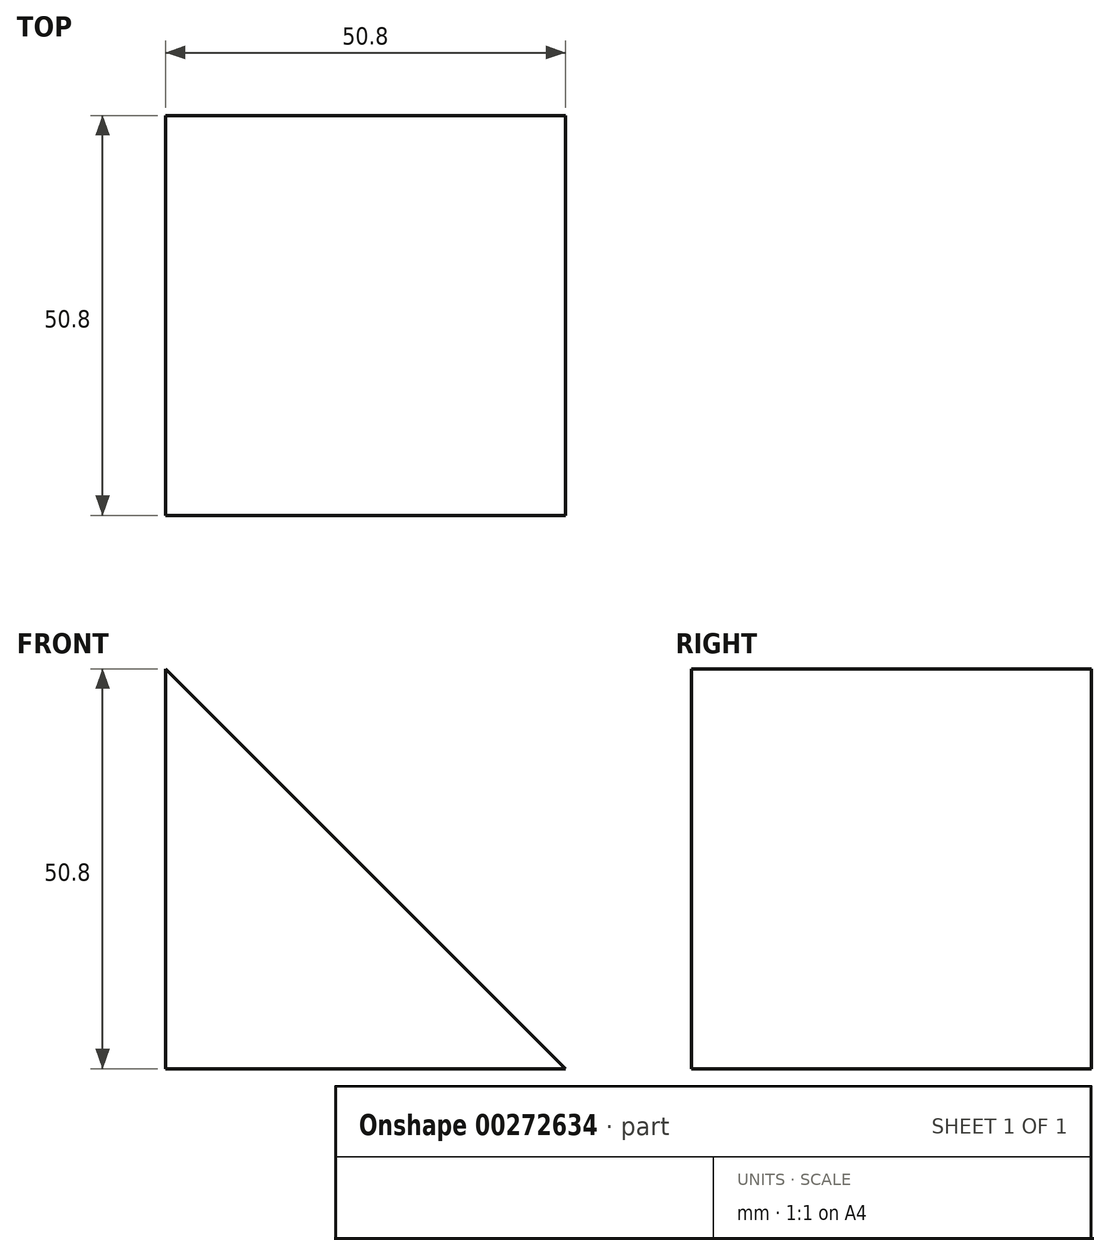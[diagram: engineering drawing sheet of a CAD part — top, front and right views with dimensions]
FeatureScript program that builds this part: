
annotation { "Feature Type Name" : "Feature", "Feature Type Description" : "" }
export const myFeature = defineFeature(function(context is Context, id is Id, definition is map)
    precondition{}
    {
        {
            var Q0;
            Q0=qCreatedBy(makeId("Front.planeOp"),FACE);
            var sketch = newSketch(context, id + "F0", { "sketchPlane" : qUnion([Q0])});
            skLineSegment(sketch, "E0.top", {"start": v(-43.73, -47.36) * mm, "end": v(7.07, -47.36) * mm});
            skLineSegment(sketch, "E0.left", {"start": v(-43.73, 3.44) * mm, "end": v(-43.73, -47.36) * mm});
            skLineSegment(sketch, "E1", {"start": v(-43.73, 3.44) * mm, "end": v(7.07, -47.36) * mm});
            skSolve(sketch);
        }
        {
            var Q0;
            Q0 = qSketchRegion(id + "F0", true);
            extrude(context, id + "F1", {"entities" : qUnion([Q0]), "depth" : 50.8 * mm});
        }
    });
